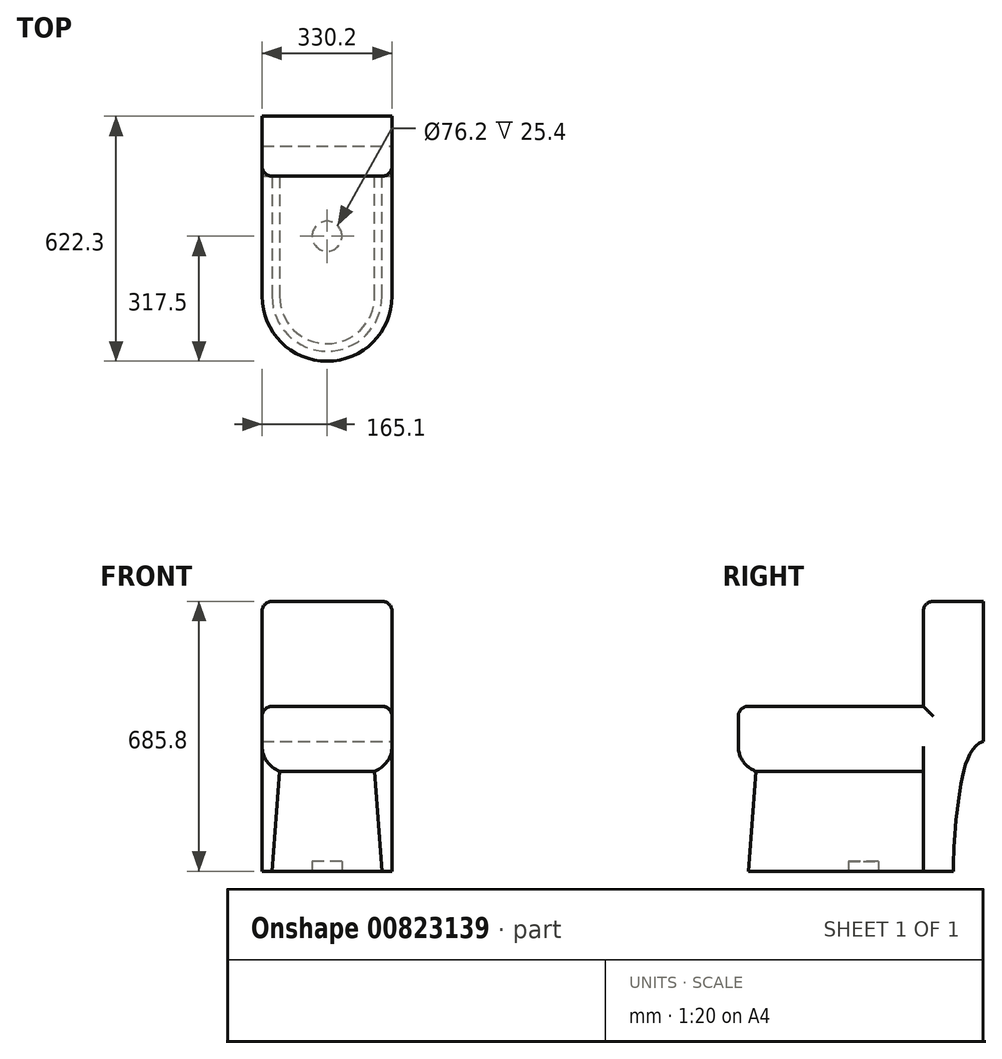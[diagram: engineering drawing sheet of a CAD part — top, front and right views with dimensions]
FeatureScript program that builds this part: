
annotation { "Feature Type Name" : "Feature", "Feature Type Description" : "" }
export const myFeature = defineFeature(function(context is Context, id is Id, definition is map)
    precondition{}
    {
        {
            var Q0;
            Q0=qCreatedBy(makeId("Top.planeOp"),FACE);
            var sketch = newSketch(context, id + "F0", { "sketchPlane" : qUnion([Q0])});
            skLineSegment(sketch, "E0", {"start": v(0, 0) * mm, "end": v(-165.1, 0) * mm});
            skLineSegment(sketch, "E1", {"start": v(-165.1, 0) * mm, "end": v(-165.1, -457.2) * mm});
            skArc(sketch, "E2", {"start": v(-165.1, -457.2) * mm, "mid": v(-116.74, -573.94) * mm, "end": v(0, -622.3) * mm});
            skLineSegment(sketch, "E3", {"start": v(0, -622.3) * mm, "end": v(0, 0) * mm});
            skLineSegment(sketch, "E4", {"start": v(-165.1, -152.4) * mm, "end": v(0, -152.4) * mm});
            skCircle(sketch, "E5", {"center": v(-101.6, -203.2) * mm, "radius": 12.7 * mm});
            skCircle(sketch, "E6", {"center": v(0, -304.8) * mm, "radius": 38.1 * mm});
            skSolve(sketch);
        }
        {
            var Q0;
            {var subQ2=sQuery(id+"F0.wireOp",EDGE,"E2");Q0=makeQuery(id+"F0.imprint","IMPRINT",FACE,{"disambiguationData":[TD([[makeQuery(id+"F0.imprint","IMPRINT",EDGE,{"derivedFrom":subQ2}),1.0]])]});}
            var Q1;
            Q1=makeQuery(id+"F0.imprint","IMPRINT",FACE,{"disambiguationData":[TD([[makeQuery(id+"F0.imprint","IMPRINT",EDGE,{"derivedFrom":sQuery(id+"F0.wireOp",EDGE,"E5")}),1.0]])]});
            var Q2;
            {var subQ0=sQuery(id+"F0.wireOp",EDGE,"E6");var subQ1=sQuery(id+"F0.wireOp",EDGE,"E3");var subQ2=makeQuery(id+"F0.imprint","INTERSECT",VERTEX,{"disambiguationData":[OD(0.0)],"derivedFrom":[subQ1,subQ0]});Q2=makeQuery(id+"F0.imprint","IMPRINT",FACE,{"disambiguationData":[TD([[makeQuery(id+"F0.imprint","IMPRINT",EDGE,{"disambiguationData":[TD([[subQ2,-1.0]])],"derivedFrom":subQ1}),1.0]])]});}
            extrude(context, id + "F1", {"entities" : qUnion([Q0, Q1, Q2]), "depth" : 419.1 * mm, "offsetDistance" : 25.4 * mm});
        }
        {
            var Q0;
            {var subQ0=sQuery(id+"F0.wireOp",EDGE,"E0");Q0=makeQuery(id+"F0.imprint","IMPRINT",FACE,{"disambiguationData":[TD([[makeQuery(id+"F0.imprint","IMPRINT",EDGE,{"derivedFrom":subQ0}),1.0]])]});}
            extrude(context, id + "F2", {"entities" : qUnion([Q0]), "operationType" : NewBodyOperationType.ADD, "depth" : 685.8 * mm, "offsetDistance" : 25.4 * mm});
        }
        {
            var Q0;
            {var subQ0=sQuery(id+"F0.wireOp",EDGE,"E6");var subQ1=sQuery(id+"F0.wireOp",EDGE,"E3");var subQ2=makeQuery(id+"F0.imprint","INTERSECT",VERTEX,{"disambiguationData":[OD(0.0)],"derivedFrom":[subQ1,subQ0]});Q0=makeQuery(id+"F0.imprint","IMPRINT",FACE,{"disambiguationData":[TD([[makeQuery(id+"F0.imprint","IMPRINT",EDGE,{"disambiguationData":[TD([[subQ2,-1.0]])],"derivedFrom":subQ1}),1.0]])]});}
            extrude(context, id + "F3", {"entities" : qUnion([Q0]), "operationType" : NewBodyOperationType.REMOVE, "depth" : 25.4 * mm, "offsetDistance" : 25.4 * mm});
        }
        {
            var Q0;
            Q0=makeQuery(id+"F1.opExtrude","SWEPT_BODY",BODY,{"disambiguationData":[OSD([sQuery(id+"F0.wireOp",EDGE,"E1"),sQuery(id+"F0.wireOp",EDGE,"E2"),sQuery(id+"F0.wireOp",EDGE,"E3"),sQuery(id+"F0.wireOp",EDGE,"E4")])]});
            var Q1;
            {var subQ0=sQuery(id+"F0.wireOp",EDGE,"E3");Q1=makeQuery(id+"F2.boolean.opBoolean","MERGE",FACE,{"derivedFrom":[makeQuery(id+"F1.opExtrude","SWEPT_FACE",FACE,{"disambiguationData":[OSD([subQ0])]}),makeQuery(id+"F2.opExtrude","SWEPT_FACE",FACE,{"disambiguationData":[OSD([subQ0])]})]});}
            mirror(context, id + "F4", {"operationType" : NewBodyOperationType.ADD, "entities" : qUnion([Q0]), "mirrorPlane" : qUnion([Q1])});
        }
        {
            var Q0;
            {var subQ0=makeQuery(id+"F2.opExtrude","SWEPT_FACE",FACE,{"disambiguationData":[OSD([sQuery(id+"F0.wireOp",EDGE,"E4")])]});Q0=makeQuery(id+"F4.boolean.opBoolean","MERGE",FACE,{"derivedFrom":[subQ0,makeQuery(id+"F4.opPattern","COPY",FACE,{"derivedFrom":subQ0,"instanceName":"1"})]});}
            var sketch = newSketch(context, id + "F5", { "sketchPlane" : qUnion([Q0])});
            skLineSegment(sketch, "E7", {"start": v(-165.1, 419.1) * mm, "end": v(-165.1, 317.5) * mm});
            skArc(sketch, "E8", {"start": v(-165.1, 317.5) * mm, "mid": v(-152.88, 278.74) * mm, "end": v(-120.65, 254) * mm});
            skLineSegment(sketch, "E9", {"start": v(-120.65, 254) * mm, "end": v(-139.7, 0) * mm});
            skLineSegment(sketch, "E10", {"start": v(-139.7, 0) * mm, "end": v(-165.1, 0) * mm});
            skLineSegment(sketch, "E11", {"start": v(-165.1, 0) * mm, "end": v(-165.1, 317.5) * mm});
            skSolve(sketch);
        }
        {
            var Q0;
            Q0=makeQuery(id+"F5.imprint","IMPRINT",FACE,{"disambiguationData":[TD([[makeQuery(id+"F5.imprint","IMPRINT",EDGE,{"derivedFrom":sQuery(id+"F5.wireOp",EDGE,"E8")}),-1.0]])]});
            var Q1;
            Q1=makeQuery(id+"F1.opExtrude","CAP_EDGE",EDGE,{"disambiguationData":[OSD([sQuery(id+"F0.wireOp",EDGE,"E1")])],"isStart":false});
            var Q2;
            {var subQ0=makeQuery(id+"F1.opExtrude","CAP_EDGE",EDGE,{"disambiguationData":[OSD([sQuery(id+"F0.wireOp",EDGE,"E2")])],"isStart":false});Q2=makeQuery(id+"F4.boolean.opBoolean","MERGE",EDGE,{"derivedFrom":[subQ0,makeQuery(id+"F4.opPattern","COPY",EDGE,{"derivedFrom":subQ0,"instanceName":"1"})]});}
            var Q3;
            Q3=makeQuery(id+"F4.opPattern","COPY",EDGE,{"derivedFrom":makeQuery(id+"F1.opExtrude","CAP_EDGE",EDGE,{"disambiguationData":[OSD([sQuery(id+"F0.wireOp",EDGE,"E1")])],"isStart":false}),"instanceName":"1"});
            sweep(context, id + "F6", {"operationType" : NewBodyOperationType.REMOVE, "profiles" : qUnion([Q0]), "path" : qUnion([Q1, Q2, Q3])});
        }
        {
            var Q0;
            Q0=qCreatedBy(makeId("Right.planeOp"),FACE);
            var sketch = newSketch(context, id + "F7", { "sketchPlane" : qUnion([Q0])});
            skFitSpline(sketch, "E12", {"points": [v(-76.2, 0) * mm, v(-62.5, 185.4) * mm, v(0, 330.2) * mm], "startDerivative": vector(0, 183.72) * mm, "endDerivative": vector(242.54, 79.48) * mm});
            skLineSegment(sketch, "E13", {"start": v(-76.2, 0) * mm, "end": v(-76.2, -28.06) * mm});
            skLineSegment(sketch, "E14", {"start": v(0, 330.2) * mm, "end": v(0, 0) * mm});
            skLineSegment(sketch, "E15", {"start": v(0, 0) * mm, "end": v(-76.2, 0) * mm});
            skSolve(sketch);
        }
        {
            var Q0;
            Q0=makeQuery(id+"F7.imprint","IMPRINT",FACE,{"disambiguationData":[TD([[makeQuery(id+"F7.imprint","IMPRINT",EDGE,{"derivedFrom":sQuery(id+"F7.wireOp",EDGE,"E12")}),-1.0]])]});
            extrude(context, id + "F8", {"entities" : qUnion([Q0]), "operationType" : NewBodyOperationType.REMOVE, "endBound" : BoundingType.THROUGH_ALL, "oppositeDirection" : true, "depth" : 25.4 * mm, "offsetDistance" : 25.4 * mm, "hasSecondDirection" : true, "secondDirectionBound" : BoundingType.THROUGH_ALL, "secondDirectionOppositeDirection" : false, "secondDirectionDepth" : 25.4 * mm});
        }
        {
            var Q0;
            Q0=makeQuery(id+"F2.opExtrude","CAP_EDGE",EDGE,{"disambiguationData":[OSD([sQuery(id+"F0.wireOp",EDGE,"E1")])],"isStart":false});
            var Q1;
            Q1=makeQuery(id+"F2.opExtrude","SWEPT_EDGE",EDGE,{"disambiguationData":[OSD([sQuery(id+"F0.wireOp",EDGE,"E1"),sQuery(id+"F0.wireOp",EDGE,"E4")])]});
            var Q2;
            {var subQ0=makeQuery(id+"F2.opExtrude","CAP_EDGE",EDGE,{"disambiguationData":[OSD([sQuery(id+"F0.wireOp",EDGE,"E4")])],"isStart":false});Q2=makeQuery(id+"F4.boolean.opBoolean","MERGE",EDGE,{"derivedFrom":[subQ0,makeQuery(id+"F4.opPattern","COPY",EDGE,{"derivedFrom":subQ0,"instanceName":"1"})]});}
            var Q3;
            Q3=makeQuery(id+"F4.opPattern","COPY",EDGE,{"derivedFrom":makeQuery(id+"F2.opExtrude","CAP_EDGE",EDGE,{"disambiguationData":[OSD([sQuery(id+"F0.wireOp",EDGE,"E1")])],"isStart":false}),"instanceName":"1"});
            var Q4;
            Q4=makeQuery(id+"F4.opPattern","COPY",EDGE,{"derivedFrom":makeQuery(id+"F2.opExtrude","SWEPT_EDGE",EDGE,{"disambiguationData":[OSD([sQuery(id+"F0.wireOp",EDGE,"E1"),sQuery(id+"F0.wireOp",EDGE,"E4")])]}),"instanceName":"1"});
            var Q5;
            Q5=makeQuery(id+"F4.opPattern","COPY",EDGE,{"derivedFrom":makeQuery(id+"F1.opExtrude","CAP_EDGE",EDGE,{"disambiguationData":[OSD([sQuery(id+"F0.wireOp",EDGE,"E1")])],"isStart":false}),"instanceName":"1"});
            var Q6;
            {var subQ0=makeQuery(id+"F1.opExtrude","CAP_EDGE",EDGE,{"disambiguationData":[OSD([sQuery(id+"F0.wireOp",EDGE,"E2")])],"isStart":false});Q6=makeQuery(id+"F4.boolean.opBoolean","MERGE",EDGE,{"derivedFrom":[subQ0,makeQuery(id+"F4.opPattern","COPY",EDGE,{"derivedFrom":subQ0,"instanceName":"1"})]});}
            var Q7;
            Q7=makeQuery(id+"F1.opExtrude","CAP_EDGE",EDGE,{"disambiguationData":[OSD([sQuery(id+"F0.wireOp",EDGE,"E1")])],"isStart":false});
            fillet(context, id + "F9", {"entities" : qUnion([Q0, Q1, Q2, Q3, Q4, Q5, Q6, Q7]), "radius" : 25.4 * mm, "tangentPropagation" : true, "allowEdgeOverflow" : false});
        }
    });
